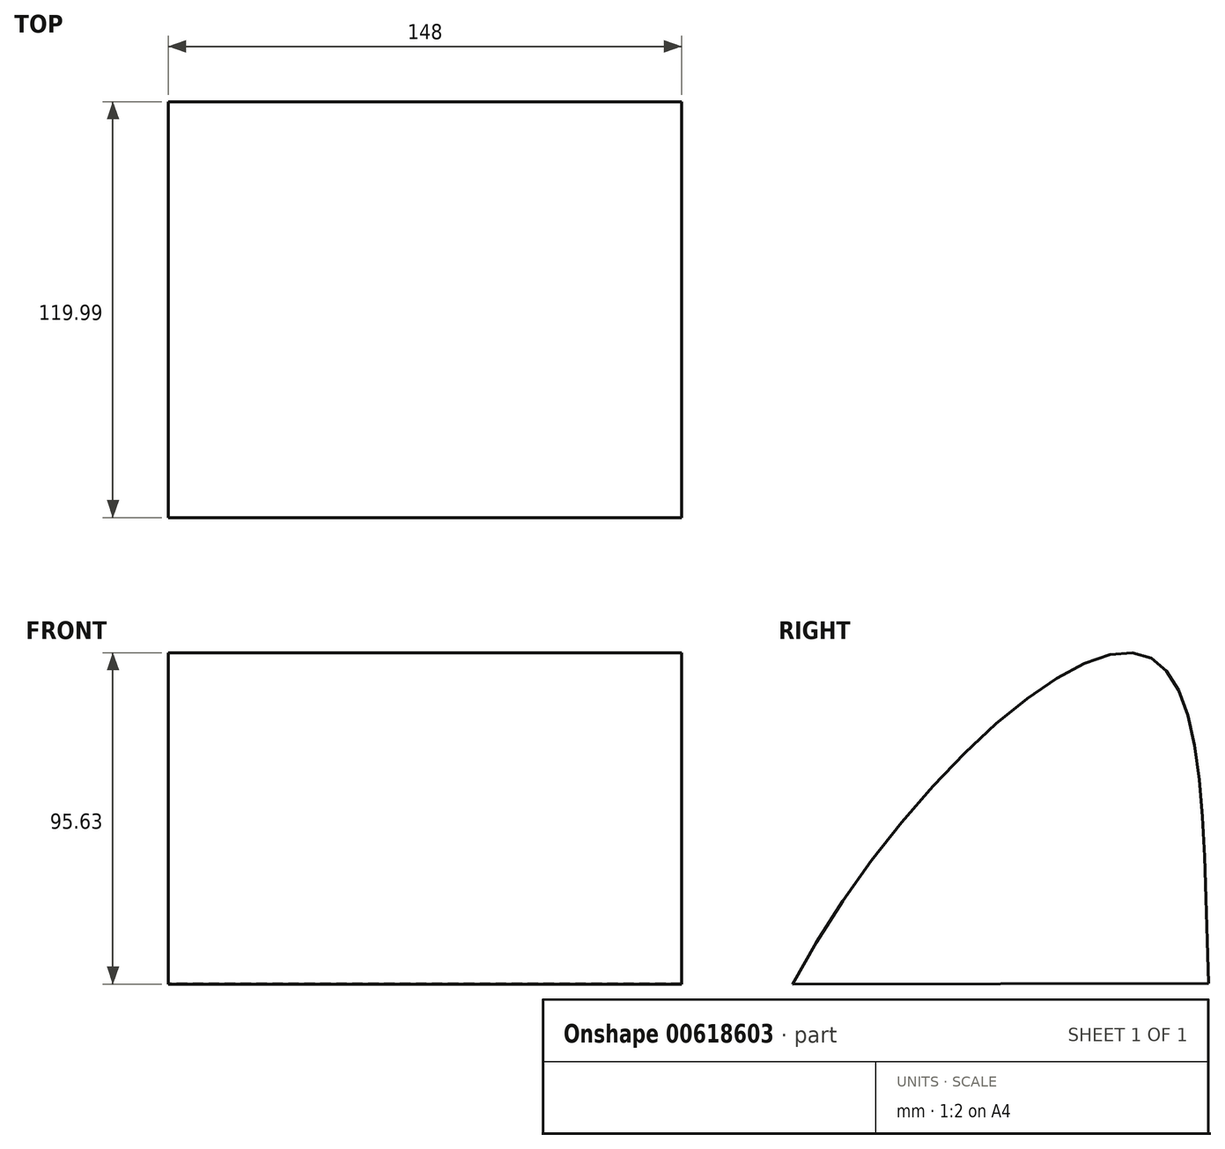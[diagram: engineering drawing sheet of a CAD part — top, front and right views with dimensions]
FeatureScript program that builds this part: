
annotation { "Feature Type Name" : "Feature", "Feature Type Description" : "" }
export const myFeature = defineFeature(function(context is Context, id is Id, definition is map)
    precondition{}
    {
        {
            var Q0;
            Q0=qCreatedBy(makeId("Right.planeOp"),FACE);
            var sketch = newSketch(context, id + "F0", { "sketchPlane" : qUnion([Q0])});
            skFitSpline(sketch, "E0", {"points": [v(-101.14, 0) * mm, v(0, 95) * mm, v(18.86, 0) * mm], "startDerivative": vector(147.2, 278.06) * mm, "endDerivative": vector(9.5, -281.01) * mm});
            skLineSegment(sketch, "E1", {"start": v(-101.14, 0) * mm, "end": v(18.86, 0) * mm});
            skFitSpline(sketch, "E2.0", {"points": [v(-106.45, 2.8) * mm, v(-103.3, 8.75) * mm, v(-96.35, 20.63) * mm, v(-84.43, 37.93) * mm, v(-71.5, 54.2) * mm, v(-58.04, 68.93) * mm, v(-46.74, 79.5) * mm, v(-37.86, 86.7) * mm, v(-31.31, 91.4) * mm, v(-24.92, 95.32) * mm, v(-18.7, 98.43) * mm, v(-12.61, 100.61) * mm, v(-7.63, 101.57) * mm, v(-3.67, 101.68) * mm, v(-1.22, 101.44) * mm, v(0.71, 101.05) * mm, v(2.14, 100.64) * mm, v(3.53, 100.12) * mm, v(5.3, 99.29) * mm, v(7.38, 98.01) * mm, v(9.6, 96.16) * mm, v(11.54, 94.05) * mm, v(13.82, 90.95) * mm, v(16.14, 86.62) * mm, v(18.29, 80.8) * mm, v(19.96, 74.37) * mm, v(21.24, 67.41) * mm, v(22.22, 59.97) * mm, v(23.2, 49.47) * mm, v(23.9, 35.45) * mm, v(24.37, 17.84) * mm, v(24.66, 6.02) * mm, v(24.85, 0.2) * mm]});
            skLineSegment(sketch, "E3", {"start": v(-106.45, 2.8) * mm, "end": v(-101.14, 0) * mm});
            skLineSegment(sketch, "E4", {"start": v(18.86, 0) * mm, "end": v(24.85, 0.2) * mm});
            skFitSpline(sketch, "E5.0", {"points": [v(-109.98, 4.68) * mm, v(-106.78, 10.73) * mm, v(-99.72, 22.79) * mm, v(-87.65, 40.31) * mm, v(-74.56, 56.8) * mm, v(-60.9, 71.74) * mm, v(-49.4, 82.5) * mm, v(-40.3, 89.87) * mm, v(-33.54, 94.72) * mm, v(-26.88, 98.81) * mm, v(-20.3, 102.1) * mm, v(-14.81, 104.08) * mm, v(-10.37, 105.12) * mm, v(-6.99, 105.59) * mm, v(-3.55, 105.69) * mm, v(-0.65, 105.41) * mm, v(1.66, 104.93) * mm, v(3.4, 104.44) * mm, v(5.07, 103.8) * mm, v(7.23, 102.8) * mm, v(9.73, 101.27) * mm, v(12.36, 99.06) * mm, v(14.64, 96.6) * mm, v(17.25, 93.04) * mm, v(19.81, 88.23) * mm, v(22.12, 81.96) * mm, v(23.87, 75.22) * mm, v(25.2, 68.03) * mm, v(26.2, 60.4) * mm, v(27.18, 49.73) * mm, v(27.9, 35.6) * mm, v(28.37, 17.93) * mm, v(28.66, 6.13) * mm, v(28.85, 0.34) * mm]});
            skLineSegment(sketch, "E6", {"start": v(24.85, 0.2) * mm, "end": v(-101.14, 0) * mm});
            skLineSegment(sketch, "E7", {"start": v(-106.45, 2.8) * mm, "end": v(-109.98, 4.68) * mm});
            skLineSegment(sketch, "E8", {"start": v(24.85, 0.2) * mm, "end": v(28.85, 0.34) * mm});
            skLineSegment(sketch, "E9", {"start": v(28.85, 0.34) * mm, "end": v(24.85, 0.2) * mm});
            skSolve(sketch);
        }
        {
            var Q0;
            Q0=makeQuery(id+"F0.imprint","IMPRINT",FACE,{"disambiguationData":[TD([[makeQuery(id+"F0.imprint","IMPRINT",EDGE,{"derivedFrom":sQuery(id+"F0.wireOp",EDGE,"E0")}),-1.0]])]});
            extrude(context, id + "F1", {"entities" : qUnion([Q0]), "depth" : 148 * mm, "offsetDistance" : 25 * mm});
        }
    });
